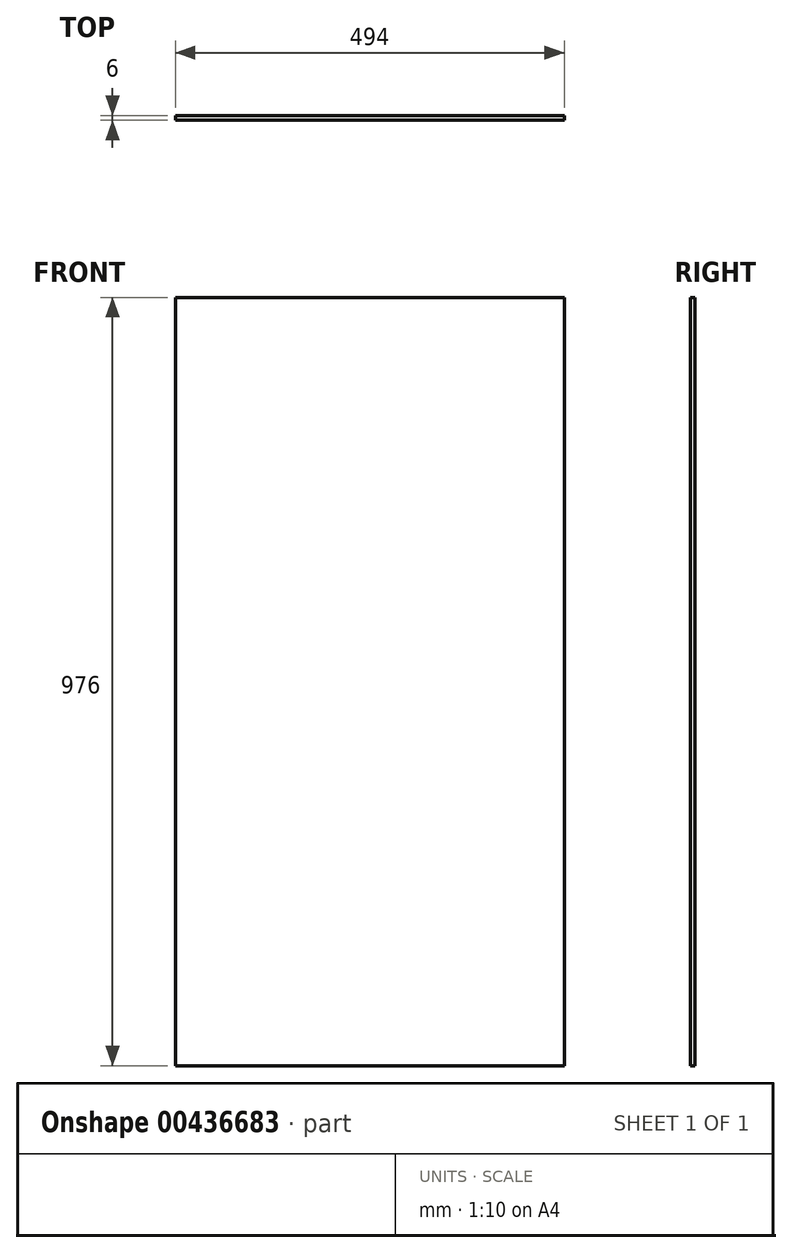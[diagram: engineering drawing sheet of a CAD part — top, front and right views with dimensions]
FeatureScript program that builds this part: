
annotation { "Feature Type Name" : "Feature", "Feature Type Description" : "" }
export const myFeature = defineFeature(function(context is Context, id is Id, definition is map)
    precondition{}
    {
        {
            var Q0;
            Q0=qCreatedBy(makeId("Front.planeOp"),FACE);
            var sketch = newSketch(context, id + "F0", { "sketchPlane" : qUnion([Q0])});
            skLineSegment(sketch, "E0.bottom", {"start": v(247, 488) * mm, "end": v(-247, 488) * mm});
            skLineSegment(sketch, "E0.top", {"start": v(247, -488) * mm, "end": v(-247, -488) * mm});
            skLineSegment(sketch, "E0.left", {"start": v(247, 488) * mm, "end": v(247, -488) * mm});
            skLineSegment(sketch, "E0.right", {"start": v(-247, 488) * mm, "end": v(-247, -488) * mm});
            skPoint(sketch, "E0.middle", {"position": v(0, 0) * mm});
            skSolve(sketch);
        }
        {
            var Q0;
            Q0 = qSketchRegion(id + "F0", true);
            extrude(context, id + "F1", {"entities" : qUnion([Q0]), "depth" : 6 * mm});
        }
    });
